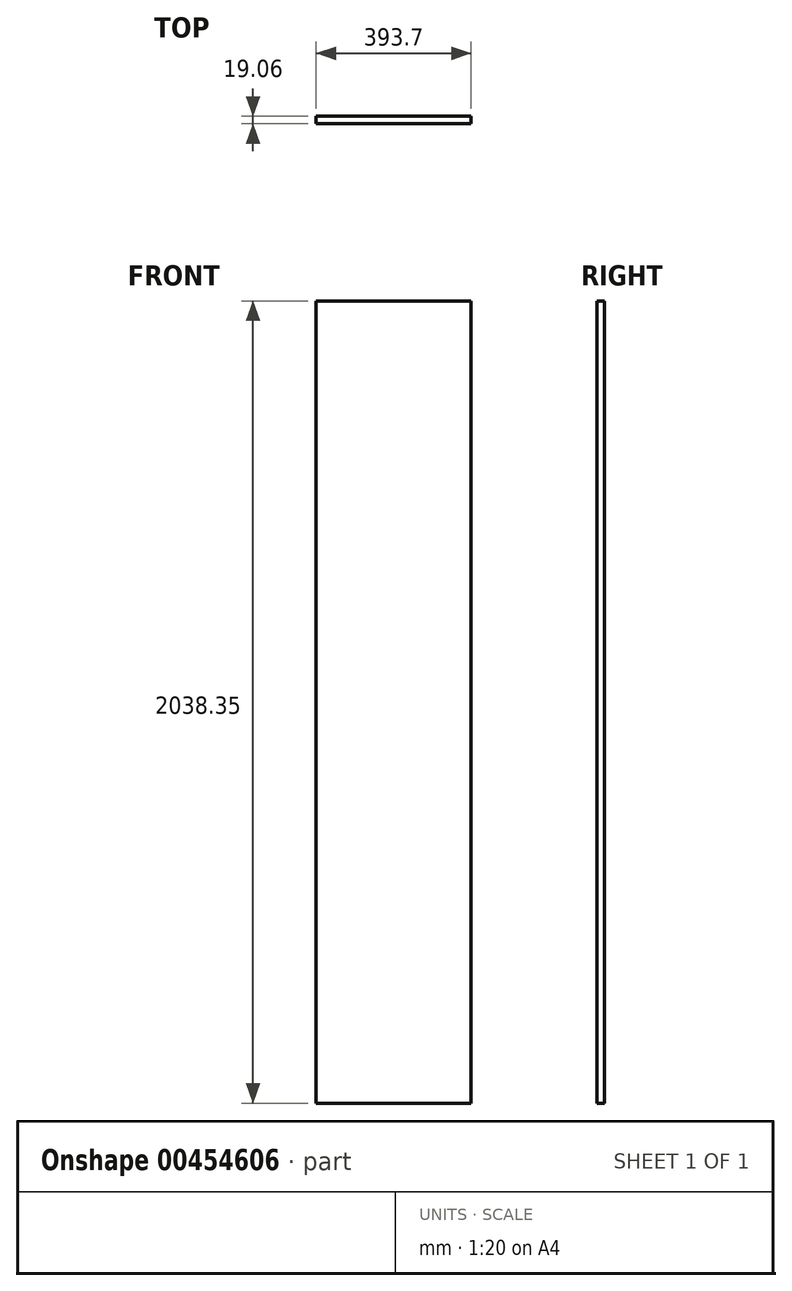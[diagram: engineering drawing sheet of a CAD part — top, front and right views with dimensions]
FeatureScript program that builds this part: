
annotation { "Feature Type Name" : "Feature", "Feature Type Description" : "" }
export const myFeature = defineFeature(function(context is Context, id is Id, definition is map)
    precondition{}
    {
        {
            var Q0;
            Q0=qCreatedBy(makeId("Top.planeOp"),FACE);
            var sketch = newSketch(context, id + "F0", { "sketchPlane" : qUnion([Q0])});
            skLineSegment(sketch, "E0.bottom", {"start": v(196.85, 9.53) * mm, "end": v(-196.85, 9.53) * mm});
            skLineSegment(sketch, "E0.top", {"start": v(196.85, -9.53) * mm, "end": v(-196.85, -9.53) * mm});
            skLineSegment(sketch, "E0.left", {"start": v(196.85, 9.53) * mm, "end": v(196.85, -9.53) * mm});
            skLineSegment(sketch, "E0.right", {"start": v(-196.85, 9.53) * mm, "end": v(-196.85, -9.53) * mm});
            skPoint(sketch, "E0.middle", {"position": v(0, 0) * mm});
            skSolve(sketch);
        }
        {
            var Q0;
            Q0=makeQuery(id+"F0.imprint","IMPRINT",FACE,{"disambiguationData":[TD([[makeQuery(id+"F0.imprint","IMPRINT",EDGE,{"derivedFrom":sQuery(id+"F0.wireOp",EDGE,"E0.bottom")}),1.0]])]});
            var Q1;
            Q1=qSketchRegion(id+"F0",true);
            extrude(context, id + "F1", {"entities" : qUnion([Q0, Q1]), "depth" : 2038.35 * mm});
        }
    });
